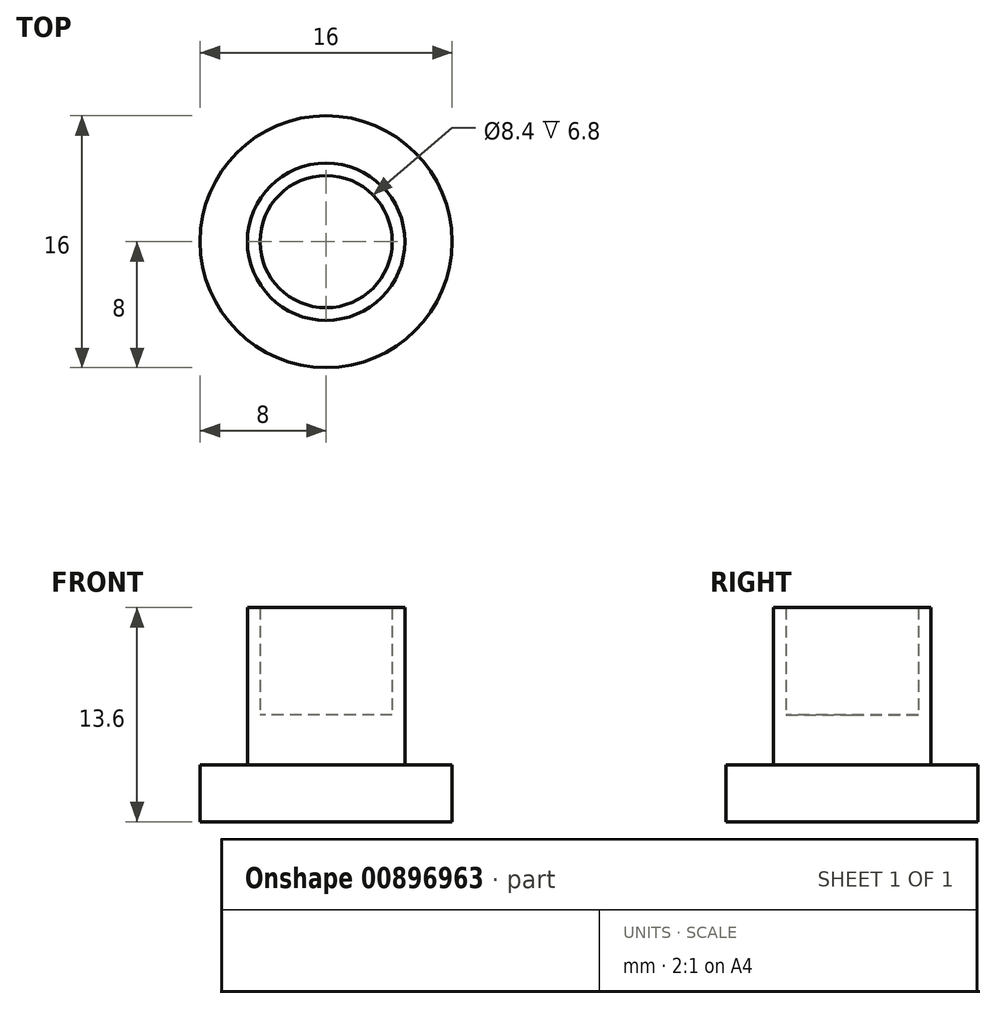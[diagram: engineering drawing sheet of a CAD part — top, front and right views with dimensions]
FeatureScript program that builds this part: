
annotation { "Feature Type Name" : "Feature", "Feature Type Description" : "" }
export const myFeature = defineFeature(function(context is Context, id is Id, definition is map)
    precondition{}
    {
        {
            var Q0;
            Q0=qCreatedBy(makeId("Top.planeOp"),FACE);
            var sketch = newSketch(context, id + "F0", { "sketchPlane" : qUnion([Q0])});
            skCircle(sketch, "E0", {"center": v(0, 0) * mm, "radius": 5 * mm});
            skSolve(sketch);
        }
        {
            var Q0;
            Q0 = qSketchRegion(id + "F0", true);
            extrude(context, id + "F1", {"entities" : qUnion([Q0]), "depth" : 3.2 * mm, "offsetDistance" : 25 * mm});
        }
        {
            var Q0;
            Q0=makeQuery(id+"F1.opExtrude","CAP_FACE",FACE,{"disambiguationData":[OSD([sQuery(id+"F0.wireOp",EDGE,"E0")])],"isStart":false});
            var sketch = newSketch(context, id + "F2", { "sketchPlane" : qUnion([Q0])});
            skCircle(sketch, "E1", {"center": v(0, 0) * mm, "radius": 4.2 * mm});
            skCircle(sketch, "E2.0", {"center": v(0, 0) * mm, "radius": 5 * mm});
            skSolve(sketch);
        }
        {
            var Q0;
            Q0 = qSketchRegion(id + "F2", true);
            extrude(context, id + "F3", {"entities" : qUnion([Q0]), "operationType" : NewBodyOperationType.ADD, "depth" : 6.8 * mm, "offsetDistance" : 25 * mm});
        }
        {
            var Q0;
            Q0=makeQuery(id+"F1.opExtrude","CAP_FACE",FACE,{"disambiguationData":[OSD([sQuery(id+"F0.wireOp",EDGE,"E0")])],"isStart":true});
            var sketch = newSketch(context, id + "F4", { "sketchPlane" : qUnion([Q0])});
            skCircle(sketch, "E3", {"center": v(0, 0) * mm, "radius": 8 * mm});
            skSolve(sketch);
        }
        {
            var Q0;
            Q0=makeQuery(id+"F4.imprint","IMPRINT",FACE,{"disambiguationData":[TD([[makeQuery(id+"F4.imprint","IMPRINT",EDGE,{"derivedFrom":makeQuery(id+"F1.opExtrude","CAP_EDGE",EDGE,{"disambiguationData":[OSD([sQuery(id+"F0.wireOp",EDGE,"E0")])],"isStart":true})}),-1.0]])]});
            var Q1;
            Q1=makeQuery(id+"F4.imprint","IMPRINT",FACE,{"disambiguationData":[TD([[makeQuery(id+"F4.imprint","IMPRINT",EDGE,{"derivedFrom":sQuery(id+"F4.wireOp",EDGE,"E3")}),1.0]])]});
            extrude(context, id + "F5", {"entities" : qUnion([Q0, Q1]), "operationType" : NewBodyOperationType.ADD, "depth" : 3.6 * mm, "offsetDistance" : 25 * mm});
        }
    });
